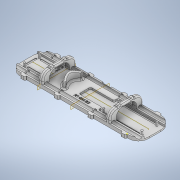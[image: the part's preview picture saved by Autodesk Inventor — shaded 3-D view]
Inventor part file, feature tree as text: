
AUTODESK INVENTOR PART (.ipt)
format: ipt  version: 2021 (Build 250183000, 183)  size: 3,036,160 bytes
history: native  units: in
note: dims shown in document units (in); Inventor stores cm internally (conversion verified against a paired STEP export)
features: sketch x14, extrude x13, fillet x11, mirror x10, plane x3, chamfer x2, revolve x1
ambient origin geometry x8: Origin, YZ Plane, XZ Plane, XY Plane, X Axis, Y Axis, Z Axis, Center Point
bodies: Solid1 (feature_tree)
feature tree (54):
  extrude  "Extrusion1"  Depth=4.9606in
  extrude  "Extrusion2"  TaperAngle=0.0deg  [1 undecoded]
  plane  "Work Plane1"
  plane  "Work Plane2"
  extrude  "Extrusion5"  Depth=0.2362in
  fillet  "Fillet2"  Radius=0.0787in
  mirror  "Mirror3"
  extrude  "Extrusion6"  TaperAngle=0.0deg  [1 undecoded]
  extrude  "Extrusion7"  Depth=0.2362in
  extrude  "Extrusion9"  [1 undecoded]
  extrude  "Extrusion10"  Depth=0.5354in
  fillet  "Fillet4"  Radius=0.9449in
  mirror  "Mirror4"
  mirror  "Mirror5"
  fillet  "Fillet5"  Radius=2.7559in
  fillet  "Fillet6"  Radius=0.4724in
  extrude  "Extrusion12"  Depth=0.0866in TaperAngle=0.0deg
  extrude  "Extrusion13"  Depth=0.0945in
  mirror  "Mirror8"
  mirror  "Mirror9"
  mirror  "Mirror10"
  fillet  "Fillet9"  Radius=0.0945in
  fillet  "Fillet11"  Radius=0.0945in
  fillet  "Fillet12"  [1 undecoded]
  extrude  "Extrusion17"  TaperAngle=0.0deg  [1 undecoded]
  fillet  "Fillet16"  [1 undecoded]
  mirror  "Mirror13"
  extrude  "Extrusion22"  Depth=1.8in
  chamfer  "Chamfer5"  Distance=0.1575in
  fillet  "Fillet29"  Radius=1.9685in
  fillet  "Fillet30"  Radius=0.9449in
  fillet  "Fillet31"  Radius=0.4724in
  extrude  "Extrusion11"  Depth=0.0945in
  revolve  "Revolution9"  [1 undecoded]
  plane  "Work Plane4"
  mirror  "Mirror16"
  mirror  "Mirror17"
  mirror  "Mirror18"
  sketch  "Sketch52"  dims[d63=1.7087in d64=0.0945in]
  extrude  "Extrusion24"  Depth=0.3937in
  chamfer  "Chamfer6"  [1 undecoded]
  sketch  "Sketch1"  dims[d0=0.1575in d1=0.0in d2=4.9606in]
  sketch  "Sketch2"  dims[d3=1.5512in d4=0.0in]
  sketch  "Sketch7"  dims[d5=0.0in d6=0.2362in d7=0.0787in d8=0.0in]
  sketch  "Sketch8"  dims[d15=-0.7756in d16=0.0in]
  sketch  "Sketch13"  dims[d17=0.0in d18=0.2362in]
  sketch  "Sketch14"  dims[d19=1.3386in d24=-2.4803in]
  sketch  "Sketch15"  dims[d28=0.5354in d29=0.0in d30=0.5354in d31=0.9449in d32=2.7559in d33=0.4724in]
  sketch  "Sketch25"  dims[d34=0.811in d35=0.0866in d36=0.0in]
  sketch  "Sketch27"  dims[d37=0.0945in d38=0.0945in d39=0.0945in d40=0.0945in d41=0.0in]
  sketch  "Sketch39"  dims[d42=0.0in d43=0.0in d44=0.0in]
  sketch  "Sketch49"  dims[d45=0.7in d46=1.8in]
  sketch  "Sketch51"  dims[d47=0.35in d48=0.1575in d49=0.0in d60=1.9685in d61=0.9449in d62=0.4724in]
  sketch  "Sketch53"  dims[d65=0.0945in d66=0.0945in d67=0.0945in d68=0.0in d69=0.0in d70=0.0in d71=0.0in d72=0.9in d73=0.7in d74=0.35in d75=0.1969in d79=0.4094in d80=0.0in d81=0.0in d82=0.0in d83=0.0in d84=0.0in d85=0.0787in d86=0.0in d88=0.3543in d89=0.315in d92=0.0394in d93=0.0in d96=1.1024in d97=0.5512in d98=0.2756in d99=0.0787in d116=0.2362in d117=0.0in d118=0.0in d119=0.1181in d120=0.0394in d121=0.0in d126=0.1575in d127=1.5748in d128=0.0in d131=0.0394in d133=0.0551in d134=0.0in d138=0.5709in d148=0.0591in d171=0.0866in d172=0.0394in d173=0.0394in d174=0.0866in d175=0.2638in d176=0.0866in d177=0.0945in d178=0.0866in d179=0.0394in d180=0.0394in d181=0.0787in d182=0.0236in d183=0.0in d184=0.0433in d204=0.0945in d240=0.0in d243=0.0in d244=0.0in d245=0.0in d246=0.1575in d247=0.1575in d248=0.315in d249=0.4724in d250=0.0in d263=0.8661in d264=0.4331in d265=0.7087in d266=0.3543in d267=0.1181in d268=0.315in d269=45.0deg d275=0.0591in d276=0.0394in d277=0.0787in d278=4.7244in d279=0.0in d280=0.0394in d281=0.0197in d282=0.0984in d284=180.0deg d285=0.0in d286=0.0in d287=0.0787in d288=-1.5748in d289=0.3937in d290=0.0472in d291=0.1969in d292=0.0787in d293=0.0in d294=0.0787in d295=0.0472in d296=45.0deg d146=0.0197in d147=0.0344in d149=0.0344in d211=0.0197in d212=0.0344in d213=0.0197in d214=0.0344in]
note: 8 required parameter values undecoded (feature->parameter linkage not recoverable at this tier; creation-order binding heuristic only, values carry confidence <= 0.55)